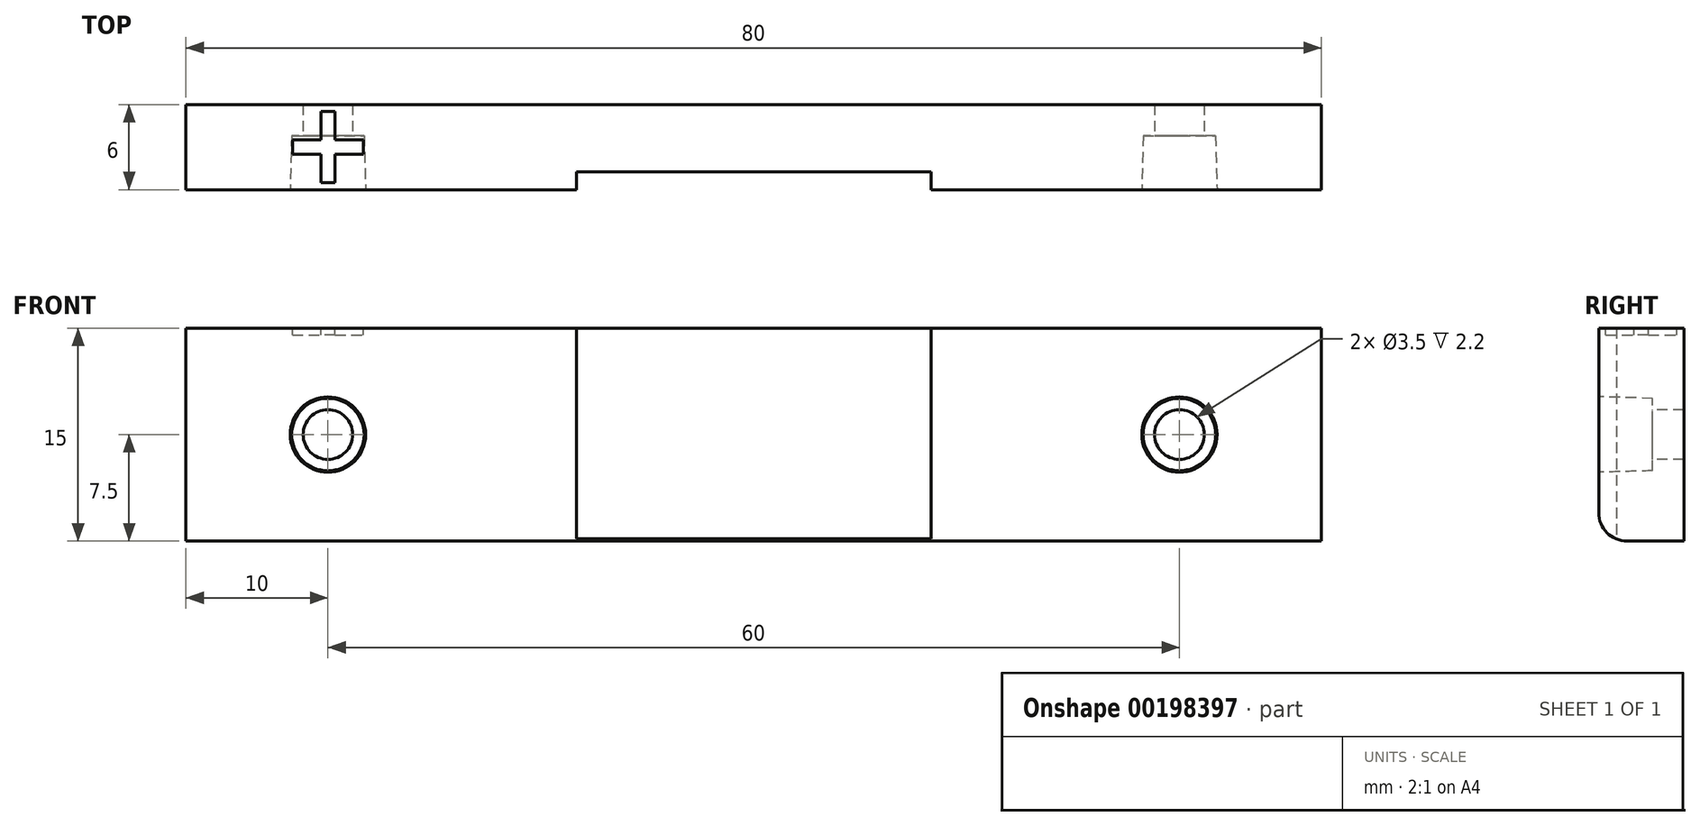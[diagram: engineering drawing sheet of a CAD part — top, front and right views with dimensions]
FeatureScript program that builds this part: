
annotation { "Feature Type Name" : "Feature", "Feature Type Description" : "" }
export const myFeature = defineFeature(function(context is Context, id is Id, definition is map)
    precondition{}
    {
        {
            var Q0;
            Q0=qCreatedBy(makeId("Top.planeOp"),FACE);
            var sketch = newSketch(context, id + "F0", { "sketchPlane" : qUnion([Q0])});
            skLineSegment(sketch, "E0.bottom", {"start": v(40, -3) * mm, "end": v(-40, -3) * mm});
            skLineSegment(sketch, "E0.top", {"start": v(40, 3) * mm, "end": v(-40, 3) * mm});
            skLineSegment(sketch, "E0.left", {"start": v(40, -3) * mm, "end": v(40, 3) * mm});
            skLineSegment(sketch, "E0.right", {"start": v(-40, -3) * mm, "end": v(-40, 3) * mm});
            skPoint(sketch, "E0.middle", {"position": v(0, 0) * mm});
            skLineSegment(sketch, "E1.bottom", {"start": v(12.5, -3) * mm, "end": v(-12.5, -3) * mm});
            skLineSegment(sketch, "E1.top", {"start": v(12.5, -1.75) * mm, "end": v(-12.5, -1.75) * mm});
            skLineSegment(sketch, "E1.left", {"start": v(12.5, -3) * mm, "end": v(12.5, -1.75) * mm});
            skLineSegment(sketch, "E1.right", {"start": v(-12.5, -3) * mm, "end": v(-12.5, -1.75) * mm});
            skPoint(sketch, "E1.middle", {"position": v(0, -2.37) * mm});
            skSolve(sketch);
        }
        {
            var Q0;
            Q0=makeQuery(id+"F0.imprint","IMPRINT",FACE,{"disambiguationData":[TD([[makeQuery(id+"F0.imprint","IMPRINT",EDGE,{"derivedFrom":sQuery(id+"F0.wireOp",EDGE,"E0.bottom")}),-1.0]])]});
            extrude(context, id + "F1", {"entities" : qUnion([Q0]), "depth" : 15 * mm});
        }
        {
            var Q0;
            Q0=makeQuery(id+"F1.opExtrude","SWEPT_FACE",FACE,{"disambiguationData":[OSD([sQuery(id+"F0.wireOp",EDGE,"E0.bottom")])]});
            var sketch = newSketch(context, id + "F2", { "sketchPlane" : qUnion([Q0])});
            skPoint(sketch, "E2", {"position": v(-30, 7.5) * mm});
            skPoint(sketch, "E3", {"position": v(30, 7.5) * mm});
            skPoint(sketch, "E4", {"position": v(0, 7.5) * mm});
            skPoint(sketch, "E4.positionSnap0", {"position": v(26.25, 0) * mm});
            skCircle(sketch, "E5", {"center": v(-30, 7.5) * mm, "radius": 2.65 * mm});
            skCircle(sketch, "E6", {"center": v(30, 7.5) * mm, "radius": 2.65 * mm});
            skSolve(sketch);
        }
        {
            var Q0;
            {var subQ0=sQuery(id+"F0.wireOp",EDGE,"E0.bottom");Q0=makeQuery(id+"F1.opExtrude","SWEPT_FACE",FACE,{"disambiguationData":[OSD([subQ0]),TDD([makeQuery(id+"F0.imprint","IMPRINT",EDGE,{"disambiguationData":[TD([[makeQuery(id+"F0.imprint","INTERSECT",VERTEX,{"derivedFrom":[subQ0,sQuery(id+"F0.wireOp",EDGE,"E0.right")]}),1.0]])],"derivedFrom":subQ0})])]});}
            cPlane(context, id + "F3", {"entities" : qUnion([Q0]), "cplaneType" : CPlaneType.OFFSET, "offset" : 3.8 * mm, "oppositeDirection" : true, "width" : 150 * mm, "height" : 150 * mm});
        }
        {
            var Q0;
            Q0=qCreatedBy(id+"F3.planeOp",FACE);
            var sketch = newSketch(context, id + "F4", { "sketchPlane" : qUnion([Q0])});
            skCircle(sketch, "E7", {"center": v(-30, 7.5) * mm, "radius": 2.55 * mm});
            skCircle(sketch, "E8", {"center": v(30, 7.5) * mm, "radius": 2.55 * mm});
            skSolve(sketch);
        }
        {
            var Q1;
            Q1=makeQuery(id+"F4.imprint","IMPRINT",FACE,{"disambiguationData":[TD([[makeQuery(id+"F4.imprint","IMPRINT",EDGE,{"derivedFrom":sQuery(id+"F4.wireOp",EDGE,"E7")}),1.0]])]});
            var Q2;
            Q2=makeQuery(id+"F2.imprint","IMPRINT",FACE,{"disambiguationData":[TD([[makeQuery(id+"F2.imprint","IMPRINT",EDGE,{"derivedFrom":sQuery(id+"F2.wireOp",EDGE,"E5")}),1.0]])]});
            var Q3;
            Q3=sQuery(id+"F4.wireOp",EDGE,"E7");
            var Q4;
            Q4=sQuery(id+"F2.wireOp",EDGE,"E5");
            loft(context, id + "F5", {"operationType" : NewBodyOperationType.REMOVE, "sheetProfilesArray" : [{ "sheetProfileEntities" : qUnion([Q1]) }, { "sheetProfileEntities" : qUnion([Q2]) }], "wireProfilesArray" : [{ "wireProfileEntities" : qUnion([Q3]) }, { "wireProfileEntities" : qUnion([Q4]) }]});
        }
        {
            var Q1;
            Q1=makeQuery(id+"F2.imprint","IMPRINT",FACE,{"disambiguationData":[TD([[makeQuery(id+"F2.imprint","IMPRINT",EDGE,{"derivedFrom":sQuery(id+"F2.wireOp",EDGE,"E6")}),1.0]])]});
            var Q2;
            Q2=makeQuery(id+"F4.imprint","IMPRINT",FACE,{"disambiguationData":[TD([[makeQuery(id+"F4.imprint","IMPRINT",EDGE,{"derivedFrom":sQuery(id+"F4.wireOp",EDGE,"E8")}),1.0]])]});
            loft(context, id + "F6", {"operationType" : NewBodyOperationType.REMOVE, "sheetProfilesArray" : [{ "sheetProfileEntities" : qUnion([Q1]) }, { "sheetProfileEntities" : qUnion([Q2]) }]});
        }
        {
            var Q0;
            Q0=sQuery(id+"F4.wireOp",VERTEX,"E8.center");
            var Q1;
            Q1=sQuery(id+"F4.wireOp",VERTEX,"E7.center");
            var Q2;
            Q2=makeQuery(id+"F1.opExtrude","SWEPT_BODY",BODY,{"disambiguationData":[OSD([sQuery(id+"F0.wireOp",EDGE,"E0.bottom"),sQuery(id+"F0.wireOp",EDGE,"E0.top"),sQuery(id+"F0.wireOp",EDGE,"E0.left"),sQuery(id+"F0.wireOp",EDGE,"E0.right")])]});
            hole(context, id + "F7", {"style" : HoleStyle.SIMPLE, "endStyle" : HoleEndStyle.THROUGH, "holeDiameter" : 3.5 * mm, "startFromSketch" : true, "locations" : qUnion([Q0, Q1]), "scope" : qUnion([Q2]), "isTappedThrough" : true});
        }
        {
            var Q0;
            Q0=makeQuery(id+"F1.opExtrude","CAP_EDGE",EDGE,{"disambiguationData":[OSD([sQuery(id+"F0.wireOp",EDGE,"E0.bottom")])],"isStart":true});
            fillet(context, id + "F8", {"entities" : qUnion([Q0]), "radius" : 2 * mm, "tangentPropagation" : true, "allowEdgeOverflow" : false});
        }
        {
            var Q0;
            Q0=makeQuery(id+"F1.opExtrude","CAP_FACE",FACE,{"disambiguationData":[OSD([sQuery(id+"F0.wireOp",EDGE,"E0.bottom"),sQuery(id+"F0.wireOp",EDGE,"E0.top"),sQuery(id+"F0.wireOp",EDGE,"E0.left"),sQuery(id+"F0.wireOp",EDGE,"E0.right")])],"isStart":false});
            var sketch = newSketch(context, id + "F9", { "sketchPlane" : qUnion([Q0])});
            skLineSegment(sketch, "E9", {"start": v(-41.58, 0) * mm, "end": v(42.12, 0) * mm, "construction": true});
            skLineSegment(sketch, "E10.bottom", {"start": v(-32.5, 0.5) * mm, "end": v(-27.5, 0.5) * mm});
            skLineSegment(sketch, "E10.top", {"start": v(-32.5, -0.5) * mm, "end": v(-27.5, -0.5) * mm});
            skLineSegment(sketch, "E10.left", {"start": v(-32.5, 0.5) * mm, "end": v(-32.5, -0.5) * mm});
            skLineSegment(sketch, "E10.right", {"start": v(-27.5, 0.5) * mm, "end": v(-27.5, -0.5) * mm});
            skPoint(sketch, "E10.middle", {"position": v(-30, 0) * mm});
            skPoint(sketch, "E11", {"position": v(-30, 0.8) * mm});
            skLineSegment(sketch, "E12", {"start": v(-30, 3.86) * mm, "end": v(-30, -3.78) * mm, "construction": true});
            skLineSegment(sketch, "E13.bottom", {"start": v(-29.5, -2.5) * mm, "end": v(-30.5, -2.5) * mm});
            skLineSegment(sketch, "E13.top", {"start": v(-29.5, 2.5) * mm, "end": v(-30.5, 2.5) * mm});
            skLineSegment(sketch, "E13.left", {"start": v(-29.5, -2.5) * mm, "end": v(-29.5, 2.5) * mm});
            skLineSegment(sketch, "E13.right", {"start": v(-30.5, -2.5) * mm, "end": v(-30.5, 2.5) * mm});
            skSolve(sketch);
        }
        {
            var Q0;
            Q0=makeQuery(id+"F9.imprint","IMPRINT",FACE,{"disambiguationData":[TD([[makeQuery(id+"F9.imprint","IMPRINT",EDGE,{"derivedFrom":sQuery(id+"F9.wireOp",EDGE,"E10.bottom")}),-1.0]])]});
            var Q1;
            {var subQ5=sQuery(id+"F9.wireOp",EDGE,"E13.top");Q1=makeQuery(id+"F9.imprint","IMPRINT",FACE,{"disambiguationData":[TD([[makeQuery(id+"F9.imprint","IMPRINT",EDGE,{"derivedFrom":subQ5}),1.0]])]});}
            var Q2;
            {var subQ5=sQuery(id+"F9.wireOp",EDGE,"E13.bottom");Q2=makeQuery(id+"F9.imprint","IMPRINT",FACE,{"disambiguationData":[TD([[makeQuery(id+"F9.imprint","IMPRINT",EDGE,{"derivedFrom":subQ5}),-1.0]])]});}
            extrude(context, id + "F10", {"entities" : qUnion([Q0, Q1, Q2]), "operationType" : NewBodyOperationType.REMOVE, "oppositeDirection" : true, "depth" : .5 * mm});
        }
    });
